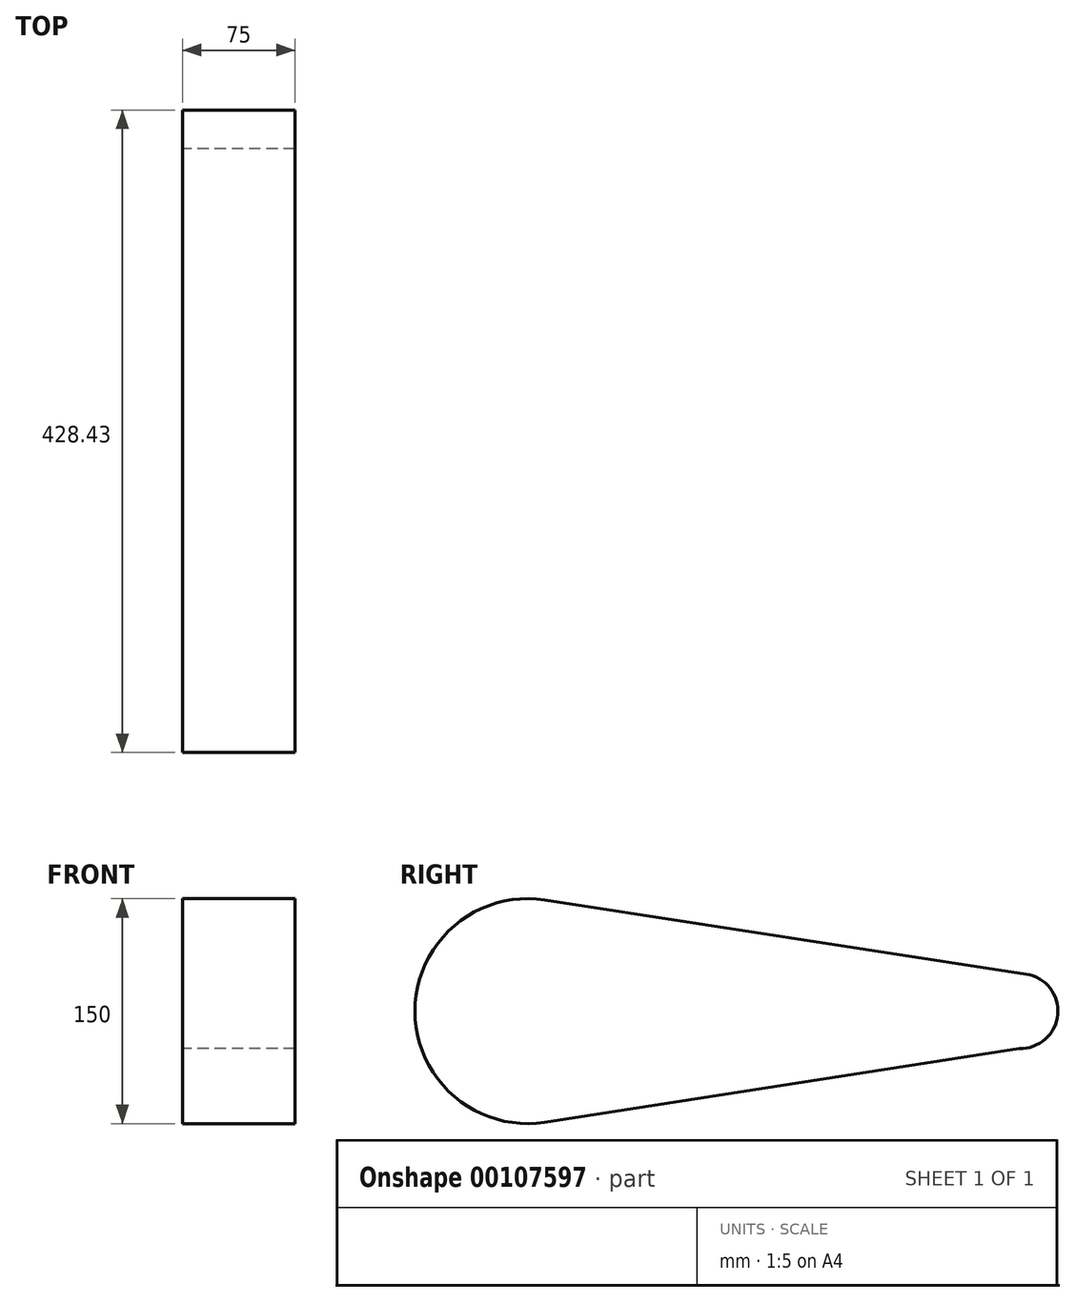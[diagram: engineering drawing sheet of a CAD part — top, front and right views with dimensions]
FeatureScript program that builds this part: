
annotation { "Feature Type Name" : "Feature", "Feature Type Description" : "" }
export const myFeature = defineFeature(function(context is Context, id is Id, definition is map)
    precondition{}
    {
        {
            var Q0;
            Q0=qCreatedBy(makeId("Right.planeOp"),FACE);
            var sketch = newSketch(context, id + "F0", { "sketchPlane" : qUnion([Q0])});
            skCircle(sketch, "E0", {"center": v(0, 0) * mm, "radius": 75 * mm});
            skLineSegment(sketch, "E1", {"start": v(11.42, 74.13) * mm, "end": v(332.24, 24.7) * mm});
            skLineSegment(sketch, "E2", {"start": v(327.6, -24.99) * mm, "end": v(11.52, -74.11) * mm});
            skCircle(sketch, "E3", {"center": v(328.43, 0) * mm, "radius": 25 * mm});
            skSolve(sketch);
        }
        {
            var Q0;
            Q0 = qSketchRegion(id + "F0", true);
            extrude(context, id + "F1", {"entities" : qUnion([Q0]), "depth" : 75 * mm});
        }
    });
